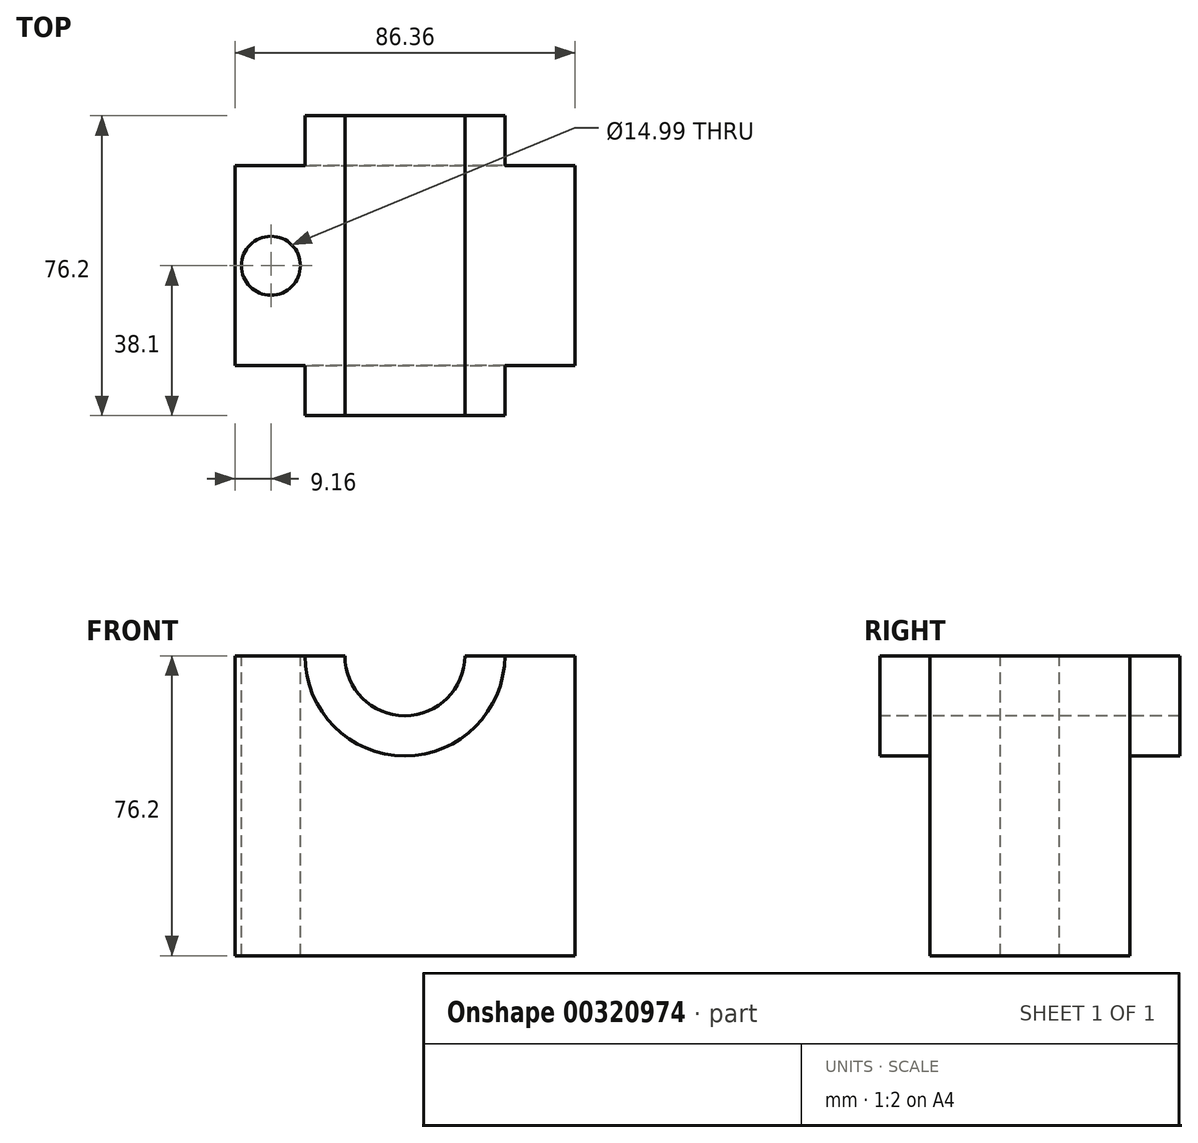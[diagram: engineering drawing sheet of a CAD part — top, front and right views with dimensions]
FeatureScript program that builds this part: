
annotation { "Feature Type Name" : "Feature", "Feature Type Description" : "" }
export const myFeature = defineFeature(function(context is Context, id is Id, definition is map)
    precondition{}
    {
        {
            var Q0;
            Q0=qCreatedBy(makeId("Top.planeOp"),FACE);
            var sketch = newSketch(context, id + "F0", { "sketchPlane" : qUnion([Q0])});
            skLineSegment(sketch, "E0", {"start": v(-43.18, -25.4) * mm, "end": v(-20.32, -25.4) * mm});
            skLineSegment(sketch, "E1", {"start": v(-43.18, -25.4) * mm, "end": v(-43.18, 0) * mm});
            skLineSegment(sketch, "E2.MirrorCS", {"start": v(-43.18, 25.4) * mm, "end": v(-20.32, 25.4) * mm});
            skLineSegment(sketch, "E3.MirrorCS", {"start": v(-43.18, 25.4) * mm, "end": v(-43.18, 0) * mm});
            skLineSegment(sketch, "E4.MirrorCS", {"start": v(43.18, -25.4) * mm, "end": v(20.32, -25.4) * mm});
            skLineSegment(sketch, "E5.MirrorCS", {"start": v(43.18, -25.4) * mm, "end": v(43.18, 0) * mm});
            skLineSegment(sketch, "E6.MirrorCS", {"start": v(43.18, 25.4) * mm, "end": v(43.18, 0) * mm});
            skLineSegment(sketch, "E7.MirrorCS", {"start": v(43.18, 25.4) * mm, "end": v(20.32, 25.4) * mm});
            skLineSegment(sketch, "E8", {"start": v(-20.32, -25.4) * mm, "end": v(20.32, -25.4) * mm});
            skLineSegment(sketch, "E9", {"start": v(-20.32, 25.4) * mm, "end": v(20.32, 25.4) * mm});
            skPoint(sketch, "E10.MirrorCS.end.orphan", {"position": v(0, 41.91) * mm});
            skPoint(sketch, "E10.MirrorCS.start.orphan", {"position": v(-20.32, 41.91) * mm});
            skPoint(sketch, "E11.MirrorCS.start.orphan", {"position": v(20.32, 41.91) * mm});
            skPoint(sketch, "E12.end.orphan", {"position": v(0, -41.91) * mm});
            skPoint(sketch, "E12.start.orphan", {"position": v(-20.32, -41.91) * mm});
            skPoint(sketch, "E13.MirrorCS.end.orphan", {"position": v(0, -41.9) * mm});
            skPoint(sketch, "E14.MirrorCS.end.orphan", {"position": v(20.32, -41.91) * mm});
            skSolve(sketch);
        }
        {
            var Q0;
            Q0=makeQuery(id+"F0.imprint","IMPRINT",FACE,{"disambiguationData":[TD([[makeQuery(id+"F0.imprint","IMPRINT",EDGE,{"derivedFrom":sQuery(id+"F0.wireOp",EDGE,"E0")}),1.0]])]});
            extrude(context, id + "F1", {"entities" : qUnion([Q0]), "endBound" : BoundingType.SYMMETRIC, "depth" : 76.2 * mm});
        }
        {
            var Q0;
            Q0=qCreatedBy(makeId("Front.planeOp"),FACE);
            var sketch = newSketch(context, id + "F2", { "sketchPlane" : qUnion([Q0])});
            skPoint(sketch, "E15", {"position": v(0, 38.1) * mm});
            skCircle(sketch, "E16", {"center": v(0, 38.1) * mm, "radius": 25.4 * mm});
            skCircle(sketch, "E17", {"center": v(0, 38.1) * mm, "radius": 15.24 * mm});
            skSolve(sketch);
        }
        {
            var Q0;
            Q0=makeQuery(id+"F2.imprint","IMPRINT",FACE,{"disambiguationData":[TD([[makeQuery(id+"F2.imprint","IMPRINT",EDGE,{"derivedFrom":sQuery(id+"F2.wireOp",EDGE,"E16")}),1.0]])]});
            extrude(context, id + "F3", {"entities" : qUnion([Q0]), "operationType" : NewBodyOperationType.ADD, "endBound" : BoundingType.SYMMETRIC, "oppositeDirection" : true, "depth" : 76.2 * mm});
        }
        {
            var Q0;
            Q0=makeQuery(id+"F3.opExtrude","CAP_FACE",FACE,{"disambiguationData":[OSD([sQuery(id+"F2.wireOp",EDGE,"E16"),sQuery(id+"F2.wireOp",EDGE,"E17")])],"isStart":true});
            var sketch = newSketch(context, id + "F4", { "sketchPlane" : qUnion([Q0])});
            skSolve(sketch);
        }
        {
            var Q0;
            Q0=makeQuery(id+"F4.imprint","IMPRINT",FACE,{"disambiguationData":[TD([[makeQuery(id+"F4.imprint","IMPRINT",EDGE,{"derivedFrom":makeQuery(id+"F3.opExtrude","CAP_EDGE",EDGE,{"disambiguationData":[OSD([sQuery(id+"F2.wireOp",EDGE,"E17")])],"isStart":true})}),1.0]])]});
            extrude(context, id + "F5", {"entities" : qUnion([Q0]), "operationType" : NewBodyOperationType.REMOVE, "oppositeDirection" : true, "depth" : 127 * mm});
        }
        {
            var Q0;
            Q0=qCreatedBy(makeId("Front.planeOp"),FACE);
            var sketch = newSketch(context, id + "F6", { "sketchPlane" : qUnion([Q0])});
            skLineSegment(sketch, "E18", {"start": v(-43.57, 38.1) * mm, "end": v(43.57, 38.1) * mm});
            skLineSegment(sketch, "E19", {"start": v(43.57, 38.1) * mm, "end": v(43.57, 71.8) * mm});
            skLineSegment(sketch, "E20", {"start": v(43.57, 71.8) * mm, "end": v(-46.03, 71.8) * mm});
            skLineSegment(sketch, "E21", {"start": v(-46.03, 71.8) * mm, "end": v(-43.57, 38.1) * mm});
            skSolve(sketch);
        }
        {
            var Q0;
            Q0=makeQuery(id+"F6.imprint","IMPRINT",FACE,{"disambiguationData":[TD([[makeQuery(id+"F6.imprint","IMPRINT",EDGE,{"derivedFrom":sQuery(id+"F6.wireOp",EDGE,"E18")}),1.0]])]});
            extrude(context, id + "F7", {"entities" : qUnion([Q0]), "operationType" : NewBodyOperationType.REMOVE, "endBound" : BoundingType.SYMMETRIC, "oppositeDirection" : true, "depth" : 127 * mm});
        }
        {
            var Q0;
            {var subQ0=sQuery(id+"F0.wireOp",EDGE,"E8");var subQ1=sQuery(id+"F0.wireOp",EDGE,"E4.MirrorCS");var subQ2=sQuery(id+"F0.wireOp",EDGE,"E0");var subQ3=sQuery(id+"F0.wireOp",EDGE,"E3.MirrorCS");var subQ4=sQuery(id+"F0.wireOp",EDGE,"E1");var subQ5=sQuery(id+"F0.wireOp",EDGE,"E9");var subQ6=sQuery(id+"F0.wireOp",EDGE,"E7.MirrorCS");var subQ7=sQuery(id+"F0.wireOp",EDGE,"E2.MirrorCS");Q0=makeQuery(id+"F7.boolean.opBoolean","MERGE",FACE,{"derivedFrom":[makeQuery(id+"F3.boolean.opBoolean","SPLIT",FACE,{"disambiguationData":[TD([makeQuery(id+"F1.opExtrude","SWEPT_FACE",FACE,{"disambiguationData":[OSD([subQ4,subQ3])]})])],"derivedFrom":makeQuery(id+"F1.opExtrude","CAP_FACE",FACE,{"disambiguationData":[OSD([subQ2,subQ4,subQ7,subQ3,subQ1,sQuery(id+"F0.wireOp",EDGE,"E5.MirrorCS"),sQuery(id+"F0.wireOp",EDGE,"E6.MirrorCS"),subQ6,subQ0,subQ5])],"isStart":false})}),makeQuery(id+"F7.opExtrude","SWEPT_FACE",FACE,{"disambiguationData":[OSD([sQuery(id+"F6.wireOp",EDGE,"E18")])]})]});}
            var sketch = newSketch(context, id + "F8", { "sketchPlane" : qUnion([Q0])});
            skCircle(sketch, "E22", {"center": v(-34.02, 0) * mm, "radius": 7.5 * mm});
            skCircle(sketch, "E23.MirrorC", {"center": v(34.02, 0) * mm, "radius": 7.5 * mm});
            skSolve(sketch);
        }
        {
            var Q0;
            Q0=makeQuery(id+"F8.imprint","IMPRINT",FACE,{"disambiguationData":[TD([[makeQuery(id+"F8.imprint","IMPRINT",EDGE,{"derivedFrom":sQuery(id+"F8.wireOp",EDGE,"E22")}),1.0]])]});
            var Q1;
            Q1=makeQuery(id+"F8.imprint","IMPRINT",FACE,{"disambiguationData":[TD([[makeQuery(id+"F8.imprint","IMPRINT",EDGE,{"derivedFrom":sQuery(id+"F8.wireOp",EDGE,"E23.MirrorC")}),-1.0]])]});
            extrude(context, id + "F9", {"entities" : qUnion([Q0, Q1]), "operationType" : NewBodyOperationType.REMOVE, "endBound" : BoundingType.THROUGH_ALL, "oppositeDirection" : true, "depth" : 25.4 * mm});
        }
    });
